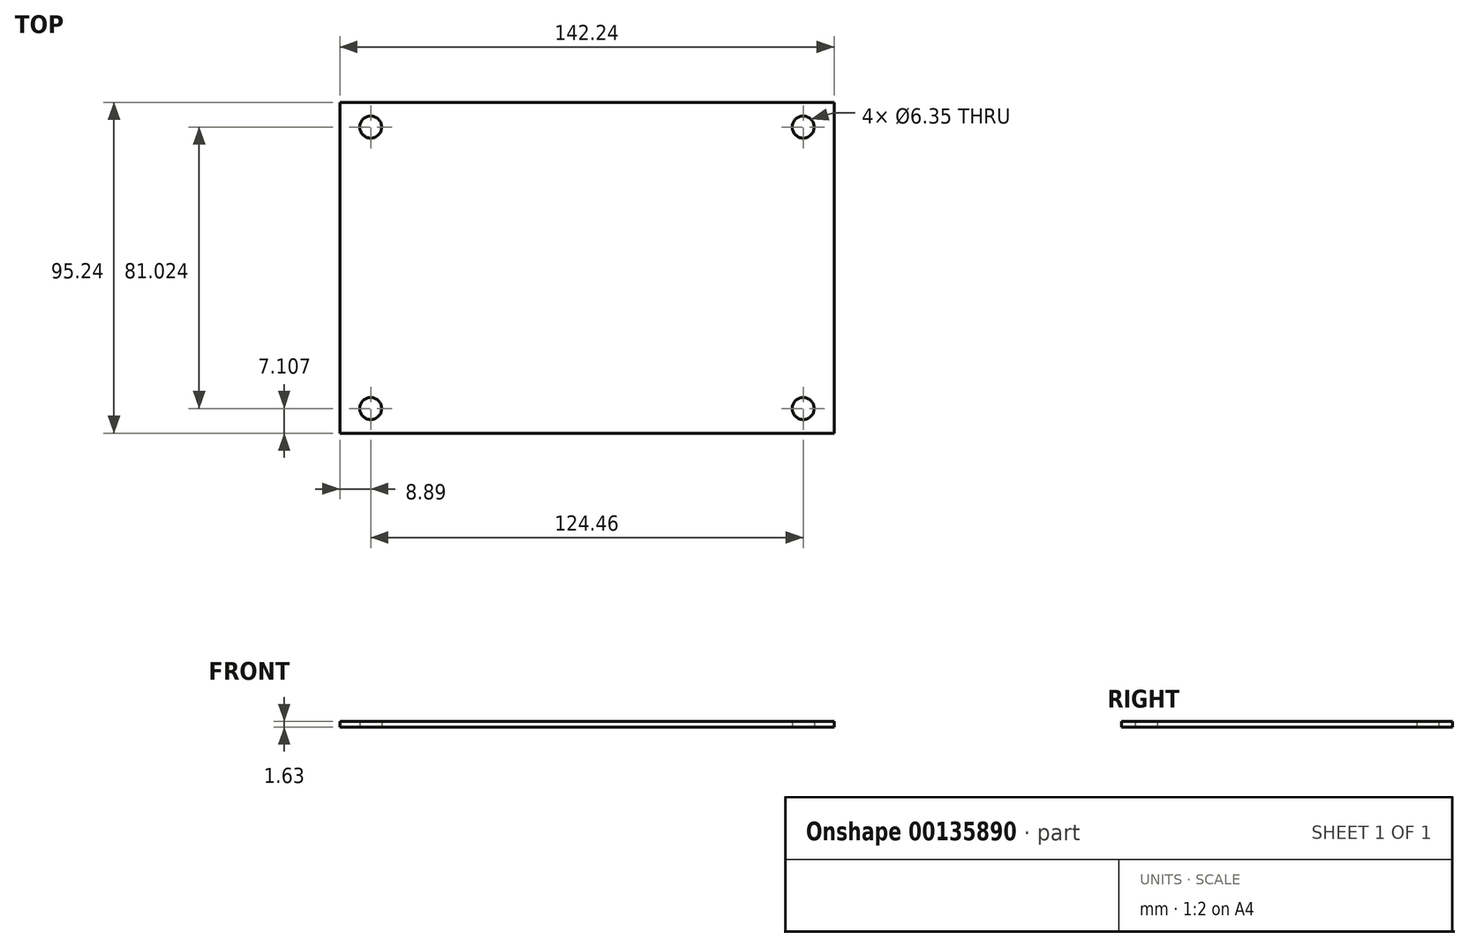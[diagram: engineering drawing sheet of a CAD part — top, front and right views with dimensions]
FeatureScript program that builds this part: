
annotation { "Feature Type Name" : "Feature", "Feature Type Description" : "" }
export const myFeature = defineFeature(function(context is Context, id is Id, definition is map)
    precondition{}
    {
        {
            var Q0;
            Q0=qCreatedBy(makeId("Top.planeOp"),FACE);
            var sketch = newSketch(context, id + "F0", { "sketchPlane" : qUnion([Q0])});
            skLineSegment(sketch, "E0.bottom", {"start": v(-71.12, -47.62) * mm, "end": v(71.12, -47.63) * mm});
            skLineSegment(sketch, "E0.top", {"start": v(-71.12, 47.63) * mm, "end": v(71.12, 47.62) * mm});
            skLineSegment(sketch, "E0.left", {"start": v(-71.12, -47.63) * mm, "end": v(-71.12, 47.62) * mm});
            skLineSegment(sketch, "E0.right", {"start": v(71.12, -47.63) * mm, "end": v(71.12, 47.63) * mm});
            skCircle(sketch, "E1", {"center": v(-62.23, 40.51) * mm, "radius": 3.18 * mm});
            skCircle(sketch, "E2", {"center": v(62.23, 40.51) * mm, "radius": 3.18 * mm});
            skCircle(sketch, "E3", {"center": v(62.23, -40.51) * mm, "radius": 3.18 * mm});
            skCircle(sketch, "E4", {"center": v(-62.23, -40.51) * mm, "radius": 3.18 * mm});
            skLineSegment(sketch, "E5", {"start": v(-71.12, 0) * mm, "end": v(71.12, 0) * mm, "construction": true});
            skLineSegment(sketch, "E6", {"start": v(0, -47.62) * mm, "end": v(0, 47.62) * mm, "construction": true});
            skPoint(sketch, "E7", {"position": v(0, 0) * mm});
            skSolve(sketch);
        }
        {
            var Q0;
            Q0 = qSketchRegion(id + "F0", true);
            extrude(context, id + "F1", {"entities" : qUnion([Q0]), "depth" : 1.63 * mm});
        }
        {
            var Q0;
            Q0=qCreatedBy(makeId("Top.planeOp"),FACE);
            cPlane(context, id + "F2", {"entities" : qUnion([Q0]), "cplaneType" : CPlaneType.OFFSET, "offset" : 8.9 * mm, "oppositeDirection" : true, "width" : 152.4 * mm, "height" : 152.4 * mm});
        }
    });
